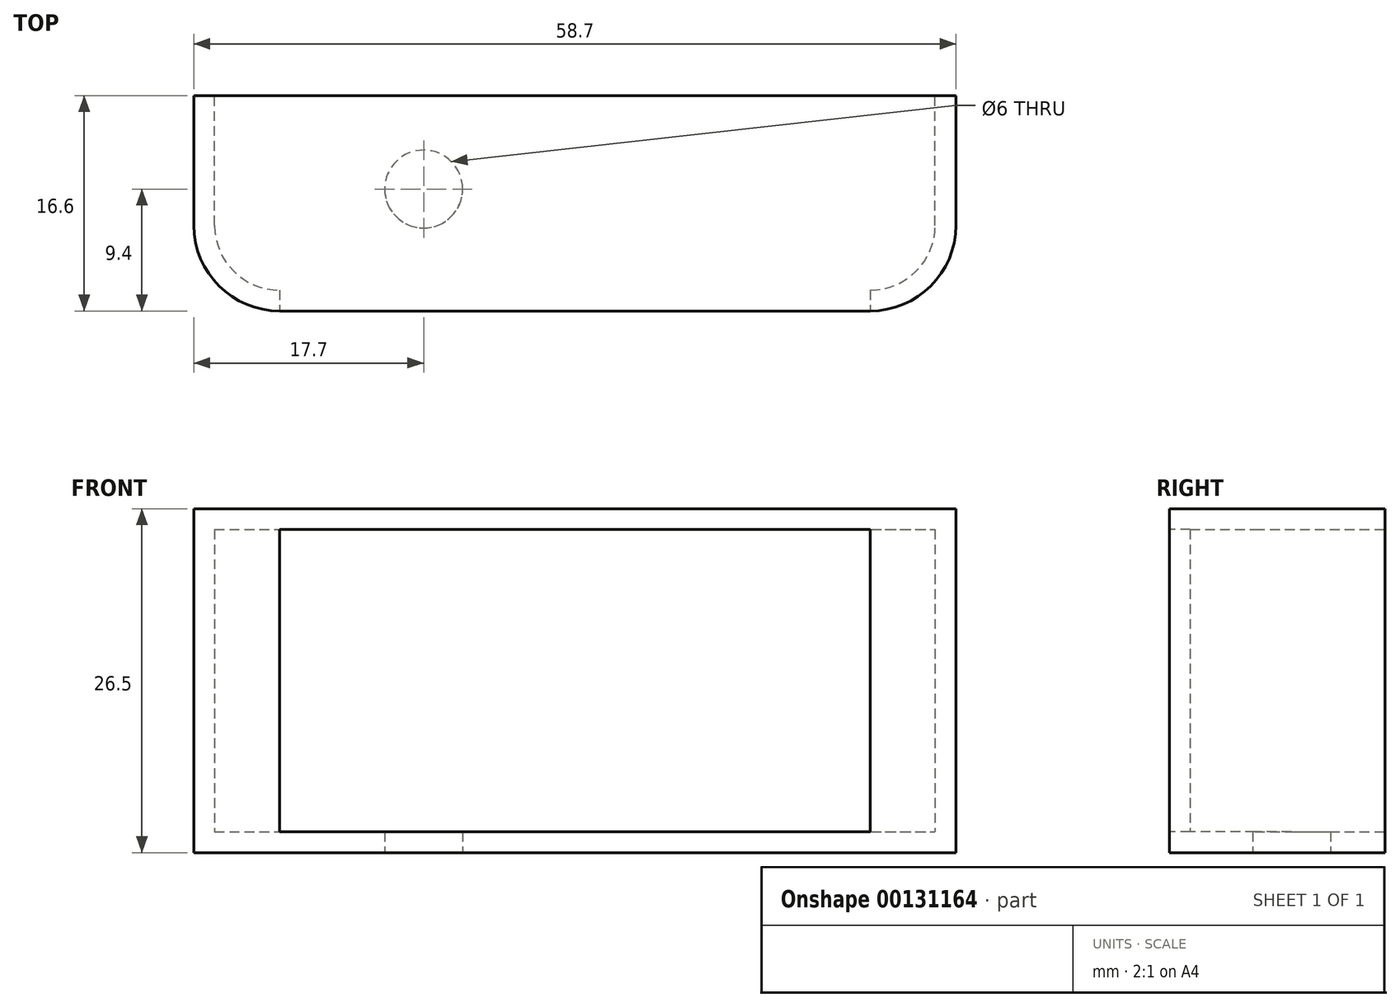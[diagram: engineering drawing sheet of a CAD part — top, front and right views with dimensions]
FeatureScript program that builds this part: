
annotation { "Feature Type Name" : "Feature", "Feature Type Description" : "" }
export const myFeature = defineFeature(function(context is Context, id is Id, definition is map)
    precondition{}
    {
        {
            var Q0;
            Q0=qCreatedBy(makeId("Top.planeOp"),FACE);
            var sketch = newSketch(context, id + "F0", { "sketchPlane" : qUnion([Q0])});
            skLineSegment(sketch, "E0.top", {"start": v(27.65, 7.5) * mm, "end": v(-27.65, 7.5) * mm});
            skPoint(sketch, "E0.middle", {"position": v(0, 0) * mm});
            skLineSegment(sketch, "E1.1", {"start": v(29.25, -9.1) * mm, "end": v(-29.25, -9.1) * mm});
            skPoint(sketch, "E0.bottom.end.orphan", {"position": v(-27.65, -7.5) * mm});
            skPoint(sketch, "E0.left.start.orphan", {"position": v(27.65, -7.5) * mm});
            skLineSegment(sketch, "E2", {"start": v(-29.25, 7.5) * mm, "end": v(-27.65, 7.5) * mm});
            skLineSegment(sketch, "E3", {"start": v(27.65, 7.5) * mm, "end": v(29.25, 7.5) * mm});
            skLineSegment(sketch, "E4.0", {"start": v(29.35, -9.1) * mm, "end": v(29.35, 7.5) * mm});
            skLineSegment(sketch, "E5.0", {"start": v(-29.35, -9.1) * mm, "end": v(-29.35, 7.5) * mm});
            skLineSegment(sketch, "E6", {"start": v(-29.25, 7.5) * mm, "end": v(-29.35, 7.5) * mm});
            skLineSegment(sketch, "E7", {"start": v(-29.25, -9.1) * mm, "end": v(-29.35, -9.1) * mm});
            skLineSegment(sketch, "E8", {"start": v(29.25, -9.1) * mm, "end": v(29.35, -9.1) * mm});
            skLineSegment(sketch, "E9", {"start": v(29.25, 7.5) * mm, "end": v(29.35, 7.5) * mm});
            skSolve(sketch);
        }
        {
            var Q0;
            Q0=qSketchRegion(id+"F0",true);
            extrude(context, id + "F1", {"entities" : qUnion([Q0]), "depth" : 26.5 * mm});
        }
        {
            var Q0;
            Q0=makeQuery(id+"F1.opExtrude","SWEPT_EDGE",EDGE,{"disambiguationData":[OSD([sQuery(id+"F0.wireOp",EDGE,"E5.0"),sQuery(id+"F0.wireOp",EDGE,"E7")])]});
            var Q1;
            Q1=makeQuery(id+"F1.opExtrude","SWEPT_EDGE",EDGE,{"disambiguationData":[OSD([sQuery(id+"F0.wireOp",EDGE,"E4.0"),sQuery(id+"F0.wireOp",EDGE,"E8")])]});
            fillet(context, id + "F2", {"entities" : qUnion([Q0, Q1]), "radius" : 6.6 * mm, "tangentPropagation" : true, "allowEdgeOverflow" : false});
        }
        {
            var Q0;
            Q0=makeQuery(id+"F1.opExtrude","SWEPT_FACE",FACE,{"disambiguationData":[OSD([sQuery(id+"F0.wireOp",EDGE,"E0.top"),sQuery(id+"F0.wireOp",EDGE,"E2"),sQuery(id+"F0.wireOp",EDGE,"E3"),sQuery(id+"F0.wireOp",EDGE,"E6"),sQuery(id+"F0.wireOp",EDGE,"E9")])]});
            shell(context, id + "F3", {"entities" : qUnion([Q0]), "thickness" : 1.6 * mm});
        }
        {
            var Q0;
            Q0=makeQuery(id+"F1.opExtrude","CAP_FACE",FACE,{"disambiguationData":[OSD([sQuery(id+"F0.wireOp",EDGE,"E0.top"),sQuery(id+"F0.wireOp",EDGE,"E1.1"),sQuery(id+"F0.wireOp",EDGE,"E2"),sQuery(id+"F0.wireOp",EDGE,"E3"),sQuery(id+"F0.wireOp",EDGE,"E4.0"),sQuery(id+"F0.wireOp",EDGE,"E5.0"),sQuery(id+"F0.wireOp",EDGE,"E6"),sQuery(id+"F0.wireOp",EDGE,"E7"),sQuery(id+"F0.wireOp",EDGE,"E8"),sQuery(id+"F0.wireOp",EDGE,"E9")])],"isStart":true});
            var sketch = newSketch(context, id + "F4", { "sketchPlane" : qUnion([Q0])});
            skLineSegment(sketch, "E10", {"start": v(29.35, -0.3) * mm, "end": v(-29.35, -0.3) * mm, "construction": true});
            skLineSegment(sketch, "E11", {"start": v(-11.65, -7.5) * mm, "end": v(-11.65, 9.1) * mm, "construction": true});
            skCircle(sketch, "E12", {"center": v(-11.65, -0.3) * mm, "radius": 3 * mm});
            skSolve(sketch);
        }
        {
            var Q0;
            Q0 = qSketchRegion(id + "F4", true);
            extrude(context, id + "F5", {"entities" : qUnion([Q0]), "operationType" : NewBodyOperationType.REMOVE, "oppositeDirection" : true, "depth" : 2 * mm});
        }
        {
            var Q0;
            Q0=makeQuery(id+"F1.opExtrude","SWEPT_FACE",FACE,{"disambiguationData":[OSD([sQuery(id+"F0.wireOp",EDGE,"E1.1"),sQuery(id+"F0.wireOp",EDGE,"E7"),sQuery(id+"F0.wireOp",EDGE,"E8")])]});
            var sketch = newSketch(context, id + "F6", { "sketchPlane" : qUnion([Q0])});
            skLineSegment(sketch, "E13.left", {"start": v(22.75, 1.6) * mm, "end": v(22.75, 24.9) * mm});
            skLineSegment(sketch, "E13.right", {"start": v(-22.75, 1.6) * mm, "end": v(-22.75, 24.9) * mm});
            skLineSegment(sketch, "E14.0", {"start": v(22.75, 1.6) * mm, "end": v(-22.75, 1.6) * mm});
            skLineSegment(sketch, "E15.0", {"start": v(22.75, 24.9) * mm, "end": v(-22.75, 24.9) * mm});
            skSolve(sketch);
        }
        {
            var Q0;
            Q0 = qSketchRegion(id + "F6", true);
            extrude(context, id + "F7", {"entities" : qUnion([Q0]), "operationType" : NewBodyOperationType.REMOVE, "oppositeDirection" : true, "depth" : 2 * mm});
        }
    });
